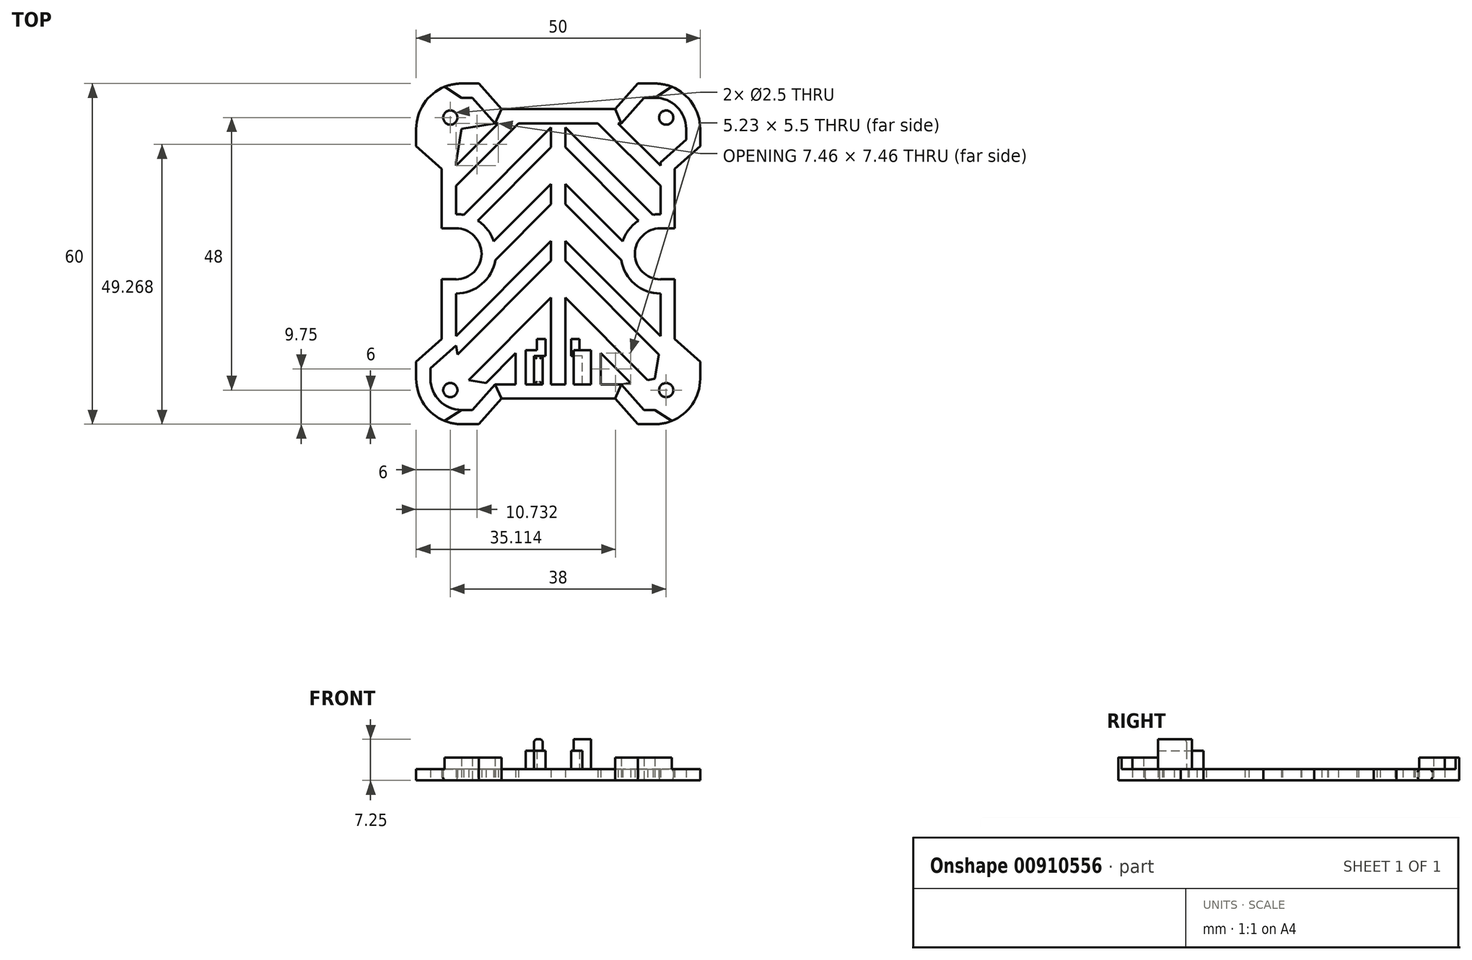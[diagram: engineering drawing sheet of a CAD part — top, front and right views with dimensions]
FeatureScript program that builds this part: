
annotation { "Feature Type Name" : "Feature", "Feature Type Description" : "" }
export const myFeature = defineFeature(function(context is Context, id is Id, definition is map)
    precondition{}
    {
        {
            var Q0;
            Q0=qCreatedBy(makeId("Top.planeOp"),FACE);
            var sketch = newSketch(context, id + "F0", { "sketchPlane" : qUnion([Q0])});
            skPoint(sketch, "E0.visualSharp", {"position": v(-25, 30) * mm});
            skArc(sketch, "E0.filletArc", {"start": v(-17, 30) * mm, "mid": v(-22.66, 27.66) * mm, "end": v(-25, 22) * mm});
            skPoint(sketch, "E1.visualSharp", {"position": v(25, 30) * mm});
            skArc(sketch, "E1.filletArc", {"start": v(25, 22) * mm, "mid": v(22.66, 27.66) * mm, "end": v(17, 30) * mm});
            skPoint(sketch, "E2.visualSharp", {"position": v(25, -30) * mm});
            skArc(sketch, "E2.filletArc", {"start": v(17, -30) * mm, "mid": v(22.66, -27.66) * mm, "end": v(25, -22) * mm});
            skPoint(sketch, "E3.visualSharp", {"position": v(-25, -30) * mm});
            skArc(sketch, "E3.filletArc", {"start": v(-25, -22) * mm, "mid": v(-22.66, -27.66) * mm, "end": v(-17, -30) * mm});
            skCircle(sketch, "E4", {"center": v(-19, 24) * mm, "radius": 1.25 * mm});
            skCircle(sketch, "E5.MirrorC", {"center": v(19, 24) * mm, "radius": 1.25 * mm});
            skCircle(sketch, "E6.MirrorC", {"center": v(19, -24) * mm, "radius": 1.25 * mm});
            skCircle(sketch, "E7.MirrorC", {"center": v(-19, -24) * mm, "radius": 1.25 * mm});
            skLineSegment(sketch, "E8", {"start": v(-10, 25.5) * mm, "end": v(10, 25.5) * mm});
            skLineSegment(sketch, "E9", {"start": v(-17, 30) * mm, "end": v(-14, 30) * mm});
            skLineSegment(sketch, "E10", {"start": v(-10, 25.5) * mm, "end": v(-14, 30) * mm});
            skLineSegment(sketch, "E11", {"start": v(10, 25.5) * mm, "end": v(14, 30) * mm});
            skLineSegment(sketch, "E12", {"start": v(-10, -25.5) * mm, "end": v(10, -25.5) * mm});
            skLineSegment(sketch, "E13", {"start": v(-17, -30) * mm, "end": v(-14, -30) * mm});
            skLineSegment(sketch, "E14", {"start": v(14, 30) * mm, "end": v(17, 30) * mm});
            skLineSegment(sketch, "E15", {"start": v(-14, -30) * mm, "end": v(-10, -25.5) * mm});
            skLineSegment(sketch, "E16", {"start": v(17, -30) * mm, "end": v(14, -30) * mm});
            skLineSegment(sketch, "E17", {"start": v(14, -30) * mm, "end": v(10, -25.5) * mm});
            skLineSegment(sketch, "E18", {"start": v(-25, -22) * mm, "end": v(-25, -19) * mm});
            skLineSegment(sketch, "E19", {"start": v(-25, 22) * mm, "end": v(-25, 19) * mm});
            skLineSegment(sketch, "E20", {"start": v(25, 22) * mm, "end": v(25, 19) * mm});
            skLineSegment(sketch, "E21", {"start": v(25, -22) * mm, "end": v(25, -19) * mm});
            skLineSegment(sketch, "E22", {"start": v(-20.5, -15) * mm, "end": v(-20.5, 15) * mm});
            skLineSegment(sketch, "E23", {"start": v(-25, -19) * mm, "end": v(-20.5, -15) * mm});
            skLineSegment(sketch, "E24", {"start": v(-20.5, 15) * mm, "end": v(-25, 19) * mm});
            skLineSegment(sketch, "E25", {"start": v(20.5, -15) * mm, "end": v(20.5, 15) * mm});
            skLineSegment(sketch, "E26", {"start": v(20.5, 15) * mm, "end": v(25, 19) * mm});
            skLineSegment(sketch, "E27", {"start": v(20.5, -15) * mm, "end": v(25, -19) * mm});
            skLineSegment(sketch, "E28", {"start": v(-10, -25.5) * mm, "end": v(-20.5, -15) * mm, "construction": true});
            skLineSegment(sketch, "E29", {"start": v(10, -25.5) * mm, "end": v(20.5, -15) * mm, "construction": true});
            skLineSegment(sketch, "E30", {"start": v(-20.5, 15) * mm, "end": v(-10, 25.5) * mm, "construction": true});
            skLineSegment(sketch, "E31", {"start": v(20.5, 15) * mm, "end": v(10, 25.5) * mm, "construction": true});
            skLineSegment(sketch, "E32.0", {"start": v(-11.12, 23) * mm, "end": v(-15.12, 27.5) * mm});
            skLineSegment(sketch, "E32.1", {"start": v(17, -27.5) * mm, "end": v(15.12, -27.5) * mm});
            skArc(sketch, "E32.2", {"start": v(17, -27.5) * mm, "mid": v(20.89, -25.89) * mm, "end": v(22.5, -22) * mm});
            skLineSegment(sketch, "E32.3", {"start": v(22.5, -22) * mm, "end": v(22.5, -20.12) * mm});
            skLineSegment(sketch, "E32.4", {"start": v(18, -16.12) * mm, "end": v(22.5, -20.12) * mm});
            skLineSegment(sketch, "E32.5", {"start": v(18, -16.12) * mm, "end": v(18, 16.12) * mm});
            skLineSegment(sketch, "E32.6", {"start": v(18, 16.12) * mm, "end": v(22.5, 20.12) * mm});
            skLineSegment(sketch, "E32.7", {"start": v(11.12, 23) * mm, "end": v(15.12, 27.5) * mm});
            skLineSegment(sketch, "E32.8", {"start": v(15.12, 27.5) * mm, "end": v(17, 27.5) * mm});
            skArc(sketch, "E32.9", {"start": v(22.5, 22) * mm, "mid": v(20.89, 25.89) * mm, "end": v(17, 27.5) * mm});
            skLineSegment(sketch, "E32.10", {"start": v(22.5, 22) * mm, "end": v(22.5, 20.12) * mm});
            skLineSegment(sketch, "E32.11", {"start": v(15.12, -27.5) * mm, "end": v(11.12, -23) * mm});
            skLineSegment(sketch, "E32.12", {"start": v(-11.12, 23) * mm, "end": v(11.12, 23) * mm});
            skLineSegment(sketch, "E32.13", {"start": v(-11.12, -23) * mm, "end": v(11.12, -23) * mm});
            skLineSegment(sketch, "E32.14", {"start": v(-15.12, -27.5) * mm, "end": v(-11.12, -23) * mm});
            skLineSegment(sketch, "E32.15", {"start": v(-17, -27.5) * mm, "end": v(-15.12, -27.5) * mm});
            skArc(sketch, "E32.16", {"start": v(-22.5, -22) * mm, "mid": v(-20.89, -25.89) * mm, "end": v(-17, -27.5) * mm});
            skLineSegment(sketch, "E32.17", {"start": v(-22.5, -22) * mm, "end": v(-22.5, -20.12) * mm});
            skLineSegment(sketch, "E32.18", {"start": v(-22.5, -20.12) * mm, "end": v(-18, -16.12) * mm});
            skLineSegment(sketch, "E32.19", {"start": v(-18, -16.12) * mm, "end": v(-18, 16.12) * mm});
            skLineSegment(sketch, "E32.20", {"start": v(-18, 16.12) * mm, "end": v(-22.5, 20.12) * mm});
            skLineSegment(sketch, "E32.21", {"start": v(-22.5, 22) * mm, "end": v(-22.5, 20.12) * mm});
            skArc(sketch, "E32.22", {"start": v(-17, 27.5) * mm, "mid": v(-20.89, 25.89) * mm, "end": v(-22.5, 22) * mm});
            skLineSegment(sketch, "E32.23", {"start": v(-17, 27.5) * mm, "end": v(-15.12, 27.5) * mm});
            skLineSegment(sketch, "E33", {"start": v(-18, 16.12) * mm, "end": v(-17, 22) * mm});
            skLineSegment(sketch, "E34", {"start": v(-11.12, 23) * mm, "end": v(-17, 22) * mm});
            skLineSegment(sketch, "E35", {"start": v(11.12, 23) * mm, "end": v(17, 22) * mm});
            skLineSegment(sketch, "E36", {"start": v(18, 16.12) * mm, "end": v(17, 22) * mm});
            skLineSegment(sketch, "E37", {"start": v(-11.12, -23) * mm, "end": v(-17, -22) * mm});
            skLineSegment(sketch, "E38", {"start": v(-18, -16.12) * mm, "end": v(-17, -22) * mm});
            skLineSegment(sketch, "E39", {"start": v(11.12, -23) * mm, "end": v(17, -22) * mm});
            skLineSegment(sketch, "E40", {"start": v(18, -16.12) * mm, "end": v(17, -22) * mm});
            skLineSegment(sketch, "E41", {"start": v(0, 3.54) * mm, "end": v(-18, -14.46) * mm});
            skLineSegment(sketch, "E42", {"start": v(0, 3.54) * mm, "end": v(18, -14.46) * mm});
            skLineSegment(sketch, "E43.0", {"start": v(-1.25, -1.25) * mm, "end": v(-17.75, -17.75) * mm});
            skLineSegment(sketch, "E43.1", {"start": v(1.25, -1.25) * mm, "end": v(17.75, -17.75) * mm});
            skLineSegment(sketch, "E44.0.1.0", {"start": v(1.25, 12.29) * mm, "end": v(18, -4.46) * mm});
            skLineSegment(sketch, "E44.0.1.1", {"start": v(1.25, 8.75) * mm, "end": v(18, -8) * mm});
            skLineSegment(sketch, "E44.0.1.2", {"start": v(-1.25, 8.75) * mm, "end": v(-18, -8) * mm});
            skLineSegment(sketch, "E44.0.1.3", {"start": v(-1.25, 12.29) * mm, "end": v(-18, -4.46) * mm});
            skLineSegment(sketch, "E44.0.2.0", {"start": v(1.25, 22.29) * mm, "end": v(18, 5.54) * mm});
            skLineSegment(sketch, "E44.0.2.1", {"start": v(1.25, 18.75) * mm, "end": v(18, 2) * mm});
            skLineSegment(sketch, "E44.0.2.2", {"start": v(-1.25, 18.75) * mm, "end": v(-18, 2) * mm});
            skLineSegment(sketch, "E44.0.2.3", {"start": v(-1.25, 22.29) * mm, "end": v(-18, 5.54) * mm});
            skLineSegment(sketch, "E44.0.3.2", {"start": v(-7, 23) * mm, "end": v(-18, 12) * mm});
            skLineSegment(sketch, "E44.0.3.3", {"start": v(-10.54, 23) * mm, "end": v(-18, 15.54) * mm});
            skLineSegment(sketch, "E44.direction1", {"start": v(18, -14.46) * mm, "end": v(43, -14.46) * mm, "construction": true});
            skLineSegment(sketch, "E44.direction2", {"start": v(18, -14.46) * mm, "end": v(18, -4.46) * mm, "construction": true});
            skLineSegment(sketch, "E45.0.1.0", {"start": v(1.25, -11.25) * mm, "end": v(12.75, -22.75) * mm});
            skLineSegment(sketch, "E45.0.1.1", {"start": v(1.25, -7.71) * mm, "end": v(15.75, -22.21) * mm});
            skLineSegment(sketch, "E45.0.1.2", {"start": v(-1.25, -7.71) * mm, "end": v(-15.75, -22.21) * mm});
            skLineSegment(sketch, "E45.0.1.3", {"start": v(-1.25, -11.25) * mm, "end": v(-12.75, -22.75) * mm});
            skLineSegment(sketch, "E45.0.2.0", {"start": v(1.25, -21.25) * mm, "end": v(3, -23) * mm});
            skLineSegment(sketch, "E45.0.2.1", {"start": v(1.25, -17.71) * mm, "end": v(6.54, -23) * mm});
            skLineSegment(sketch, "E45.0.2.2", {"start": v(-1.25, -17.71) * mm, "end": v(-6.54, -23) * mm});
            skLineSegment(sketch, "E45.0.2.3", {"start": v(-1.25, -21.25) * mm, "end": v(-3, -23) * mm});
            skLineSegment(sketch, "E45.direction1", {"start": v(18, -18) * mm, "end": v(43, -18) * mm, "construction": true});
            skLineSegment(sketch, "E45.direction2", {"start": v(18, -18) * mm, "end": v(18, -28) * mm, "construction": true});
            skPoint(sketch, "E46.orphan", {"position": v(-18, -34.46) * mm});
            skPoint(sketch, "E47.orphan", {"position": v(-18, -38) * mm});
            skPoint(sketch, "E48.orphan", {"position": v(18, -34.46) * mm});
            skLineSegment(sketch, "E49.trimOffspring", {"start": v(7, 23) * mm, "end": v(18, 12) * mm});
            skLineSegment(sketch, "E50.trimOffspring", {"start": v(10.54, 23) * mm, "end": v(18, 15.54) * mm});
            skPoint(sketch, "E51.orphan", {"position": v(0, 30) * mm});
            skPoint(sketch, "E52.orphan", {"position": v(0, 33.54) * mm});
            skPoint(sketch, "E53.orphan", {"position": v(0, 23.54) * mm});
            skLineSegment(sketch, "E54.bottom", {"start": v(-1.25, 23) * mm, "end": v(1.25, 23) * mm});
            skLineSegment(sketch, "E54.top", {"start": v(-1.25, -23) * mm, "end": v(1.25, -23) * mm});
            skLineSegment(sketch, "E54.left", {"start": v(-1.25, 23) * mm, "end": v(-1.25, -23) * mm});
            skLineSegment(sketch, "E54.right", {"start": v(1.25, 23) * mm, "end": v(1.25, -23) * mm});
            skPoint(sketch, "E54.middle", {"position": v(0, 0) * mm});
            skPoint(sketch, "E55.orphan", {"position": v(0, 20) * mm});
            skPoint(sketch, "E56.orphan", {"position": v(0, 13.54) * mm});
            skPoint(sketch, "E57.orphan", {"position": v(0, 10) * mm});
            skPoint(sketch, "E58.orphan", {"position": v(0, -20) * mm});
            skPoint(sketch, "E59.orphan", {"position": v(0, -16.46) * mm});
            skPoint(sketch, "E60.orphan", {"position": v(0, -10) * mm});
            skPoint(sketch, "E61.orphan", {"position": v(0, -6.46) * mm});
            skLineSegment(sketch, "E62", {"start": v(-7.5, -23) * mm, "end": v(-7.5, -17.5) * mm});
            skLineSegment(sketch, "E63.MirrorCS", {"start": v(7.5, -23) * mm, "end": v(7.5, -17.5) * mm});
            skLineSegment(sketch, "E64", {"start": v(-11.12, 23) * mm, "end": v(-10, 25.5) * mm});
            skLineSegment(sketch, "E65", {"start": v(-17, 27.5) * mm, "end": v(-20, 29.42) * mm});
            skLineSegment(sketch, "E66", {"start": v(11.12, 23) * mm, "end": v(10, 25.5) * mm});
            skLineSegment(sketch, "E67", {"start": v(17, 27.5) * mm, "end": v(20, 29.42) * mm});
            skLineSegment(sketch, "E68", {"start": v(-10, -25.5) * mm, "end": v(-11.12, -23) * mm});
            skLineSegment(sketch, "E69", {"start": v(10, -25.5) * mm, "end": v(11.12, -23) * mm});
            skLineSegment(sketch, "E70", {"start": v(-17, -27.5) * mm, "end": v(-20, -29.42) * mm});
            skLineSegment(sketch, "E71", {"start": v(17, -27.5) * mm, "end": v(20, -29.42) * mm});
            skArc(sketch, "E72.trimOffspring", {"start": v(-18, -7) * mm, "mid": v(-11, 0) * mm, "end": v(-18, 7) * mm});
            skArc(sketch, "E73.trimOffspring", {"start": v(-18, -4.5) * mm, "mid": v(-13.5, 0) * mm, "end": v(-18, 4.5) * mm});
            skLineSegment(sketch, "E74", {"start": v(-18, 7) * mm, "end": v(-20.5, 7) * mm});
            skLineSegment(sketch, "E75", {"start": v(-18, 4.5) * mm, "end": v(-20.5, 4.5) * mm});
            skLineSegment(sketch, "E76", {"start": v(-18, -7) * mm, "end": v(-20.5, -7) * mm});
            skLineSegment(sketch, "E77", {"start": v(-18, -4.46) * mm, "end": v(-20.5, -4.46) * mm});
            skArc(sketch, "E78.MirrorCS", {"start": v(18, -4.5) * mm, "mid": v(13.5, 0) * mm, "end": v(18, 4.5) * mm});
            skArc(sketch, "E79.MirrorCS", {"start": v(18, -7) * mm, "mid": v(11, 0) * mm, "end": v(18, 7) * mm});
            skLineSegment(sketch, "E80.MirrorCS", {"start": v(18, 4.5) * mm, "end": v(20.5, 4.5) * mm});
            skLineSegment(sketch, "E81.MirrorCS", {"start": v(18, 7) * mm, "end": v(20.5, 7) * mm});
            skLineSegment(sketch, "E82.MirrorCS", {"start": v(18, -7) * mm, "end": v(20.5, -7) * mm});
            skLineSegment(sketch, "E83.MirrorCS", {"start": v(18, -4.46) * mm, "end": v(20.5, -4.46) * mm});
            skSolve(sketch);
        }
        {
            var Q0;
            Q0=makeQuery(id+"F0.imprint","IMPRINT",FACE,{"disambiguationData":[TD([[makeQuery(id+"F0.imprint","IMPRINT",EDGE,{"derivedFrom":sQuery(id+"F0.wireOp",EDGE,"qVhlgd7Z-K8wA-2s9c-4Va0-7I31SFR7jzgF.bottom")}),-1.0]])]});
            var Q1;
            {var subQ1=sQuery(id+"F0.wireOp",EDGE,"bAQaguaC-gw7z-6hSp-WNjj-it6Kwomhn3MH.bottom");var subQ4=sQuery(id+"F0.wireOp",EDGE,"bAQaguaC-gw7z-6hSp-WNjj-it6Kwomhn3MH.left");var subQ9=makeQuery(id+"F0.imprint","INTERSECT",VERTEX,{"derivedFrom":[subQ1,subQ4]});Q1=makeQuery(id+"F0.imprint","IMPRINT",FACE,{"disambiguationData":[TD([[makeQuery(id+"F0.imprint","IMPRINT",EDGE,{"disambiguationData":[TD([[subQ9,-1.0]])],"derivedFrom":subQ1}),-1.0]])]});}
            var Q2;
            {var subQ0=sQuery(id+"F0.wireOp",EDGE,"3b41a42e-ea02-44ec-bd11-05c8cb4d84110.MirrorCS");Q2=makeQuery(id+"F0.imprint","IMPRINT",FACE,{"disambiguationData":[TD([[makeQuery(id+"F0.imprint","IMPRINT",EDGE,{"derivedFrom":subQ0}),-1.0]])]});}
            var Q3;
            Q3=makeQuery(id+"F0.imprint","IMPRINT",FACE,{"disambiguationData":[TD([[makeQuery(id+"F0.imprint","IMPRINT",EDGE,{"derivedFrom":sQuery(id+"F0.wireOp",EDGE,"5EblEZfn-I8Wa-IbvZ-PO4Y-9xLoYuIDBuYk.bottom")}),-1.0]])]});
            var Q4;
            {var subQ0=sQuery(id+"F0.wireOp",EDGE,"252a318b-4038-41aa-b63b-639a4f701ae30.MirrorCS");Q4=makeQuery(id+"F0.imprint","IMPRINT",FACE,{"disambiguationData":[TD([[makeQuery(id+"F0.imprint","IMPRINT",EDGE,{"derivedFrom":subQ0}),1.0]])]});}
            var Q5;
            {var subQ0=sQuery(id+"F0.wireOp",EDGE,"58b98b9d-614e-4e5d-8269-9d4372af3b9f0.MirrorCS");Q5=makeQuery(id+"F0.imprint","IMPRINT",FACE,{"disambiguationData":[TD([[makeQuery(id+"F0.imprint","IMPRINT",EDGE,{"derivedFrom":subQ0}),-1.0]])]});}
            var Q6;
            Q6=makeQuery(id+"F0.imprint","IMPRINT",FACE,{"disambiguationData":[TD([[makeQuery(id+"F0.imprint","IMPRINT",EDGE,{"derivedFrom":sQuery(id+"F0.wireOp",EDGE,"E0.filletArc")}),1.0]])]});
            var Q7;
            Q7=makeQuery(id+"F0.imprint","IMPRINT",FACE,{"disambiguationData":[TD([[makeQuery(id+"F0.imprint","IMPRINT",EDGE,{"derivedFrom":sQuery(id+"F0.wireOp",EDGE,"xvgLrtku-wdkR-8HBo-YxuC-FjmSOnXhvL37")}),-1.0]])]});
            var Q8;
            Q8=makeQuery(id+"F0.imprint","IMPRINT",FACE,{"disambiguationData":[TD([[makeQuery(id+"F0.imprint","IMPRINT",EDGE,{"derivedFrom":sQuery(id+"F0.wireOp",EDGE,"E10")}),1.0]])]});
            var Q9;
            Q9=makeQuery(id+"F0.imprint","IMPRINT",FACE,{"disambiguationData":[TD([[makeQuery(id+"F0.imprint","IMPRINT",EDGE,{"derivedFrom":sQuery(id+"F0.wireOp",EDGE,"5909cff1-2e5d-4e63-b456-f55076b46f4d0.MirrorCS")}),-1.0]])]});
            var Q10;
            Q10=makeQuery(id+"F0.imprint","IMPRINT",FACE,{"disambiguationData":[TD([[makeQuery(id+"F0.imprint","IMPRINT",EDGE,{"derivedFrom":sQuery(id+"F0.wireOp",EDGE,"86012b31-d1bc-4a6e-bdbf-ee867ae8a5b00.MirrorCS")}),1.0]])]});
            var Q11;
            Q11=makeQuery(id+"F0.imprint","IMPRINT",FACE,{"disambiguationData":[TD([[makeQuery(id+"F0.imprint","IMPRINT",EDGE,{"derivedFrom":sQuery(id+"F0.wireOp",EDGE,"afaa9ab5-ff9c-4d97-af4b-f4bc579a4ab80.MirrorCS")}),-1.0]])]});
            var Q12;
            {var subQ0=sQuery(id+"F0.wireOp",EDGE,"E44.0.3.2");Q12=makeQuery(id+"F0.imprint","IMPRINT",FACE,{"disambiguationData":[TD([[makeQuery(id+"F0.imprint","IMPRINT",EDGE,{"derivedFrom":subQ0}),-1.0]])]});}
            var Q13;
            {var subQ0=sQuery(id+"F0.wireOp",EDGE,"E49.trimOffspring");Q13=makeQuery(id+"F0.imprint","IMPRINT",FACE,{"disambiguationData":[TD([[makeQuery(id+"F0.imprint","IMPRINT",EDGE,{"derivedFrom":subQ0}),1.0]])]});}
            var Q14;
            {var subQ0=sQuery(id+"F0.wireOp",EDGE,"E45.0.1.1");Q14=makeQuery(id+"F0.imprint","IMPRINT",FACE,{"disambiguationData":[TD([[makeQuery(id+"F0.imprint","IMPRINT",EDGE,{"derivedFrom":subQ0}),-1.0]])]});}
            var Q15;
            {var subQ1=sQuery(id+"F0.wireOp",EDGE,"E45.0.2.0");Q15=makeQuery(id+"F0.imprint","IMPRINT",FACE,{"disambiguationData":[TD([[makeQuery(id+"F0.imprint","IMPRINT",EDGE,{"derivedFrom":subQ1}),1.0]])]});}
            var Q16;
            {var subQ3=sQuery(id+"F0.wireOp",EDGE,"E41");Q16=makeQuery(id+"F0.imprint","IMPRINT",FACE,{"disambiguationData":[TD([[makeQuery(id+"F0.imprint","IMPRINT",EDGE,{"derivedFrom":subQ3}),1.0]])]});}
            var Q17;
            {var subQ0=sQuery(id+"F0.wireOp",EDGE,"E44.0.2.0");Q17=makeQuery(id+"F0.imprint","IMPRINT",FACE,{"disambiguationData":[TD([[makeQuery(id+"F0.imprint","IMPRINT",EDGE,{"derivedFrom":subQ0}),-1.0]])]});}
            var Q18;
            Q18=makeQuery(id+"F0.imprint","IMPRINT",FACE,{"disambiguationData":[TD([[makeQuery(id+"F0.imprint","IMPRINT",EDGE,{"derivedFrom":sQuery(id+"F0.wireOp",EDGE,"E6.MirrorC")}),-1.0]])]});
            var Q19;
            Q19=makeQuery(id+"F0.imprint","IMPRINT",FACE,{"disambiguationData":[TD([[makeQuery(id+"F0.imprint","IMPRINT",EDGE,{"derivedFrom":sQuery(id+"F0.wireOp",EDGE,"E5.MirrorC")}),1.0]])]});
            var Q20;
            Q20=makeQuery(id+"F0.imprint","IMPRINT",FACE,{"disambiguationData":[TD([[makeQuery(id+"F0.imprint","IMPRINT",EDGE,{"derivedFrom":sQuery(id+"F0.wireOp",EDGE,"E4")}),-1.0]])]});
            var Q21;
            Q21=makeQuery(id+"F0.imprint","IMPRINT",FACE,{"disambiguationData":[TD([[makeQuery(id+"F0.imprint","IMPRINT",EDGE,{"derivedFrom":sQuery(id+"F0.wireOp",EDGE,"E7.MirrorC")}),1.0]])]});
            var Q22;
            {var subQ13=sQuery(id+"F0.wireOp",EDGE,"E54.top");Q22=makeQuery(id+"F0.imprint","IMPRINT",FACE,{"disambiguationData":[TD([[makeQuery(id+"F0.imprint","IMPRINT",EDGE,{"derivedFrom":subQ13}),1.0]])]});}
            var Q23;
            {var subQ5=sQuery(id+"F0.wireOp",EDGE,"E42");var subQ6=sQuery(id+"F0.wireOp",EDGE,"E32.5");var subQ7=makeQuery(id+"F0.imprint","INTERSECT",VERTEX,{"derivedFrom":[subQ6,subQ5]});Q23=makeQuery(id+"F0.imprint","IMPRINT",FACE,{"disambiguationData":[TD([[makeQuery(id+"F0.imprint","IMPRINT",EDGE,{"disambiguationData":[TD([[subQ7,1.0]])],"derivedFrom":subQ5}),-1.0]])]});}
            var Q24;
            {var subQ0=sQuery(id+"F0.wireOp",EDGE,"E45.0.1.2");Q24=makeQuery(id+"F0.imprint","IMPRINT",FACE,{"disambiguationData":[TD([[makeQuery(id+"F0.imprint","IMPRINT",EDGE,{"derivedFrom":subQ0}),1.0]])]});}
            var Q25;
            {var subQ0=sQuery(id+"F0.wireOp",EDGE,"E45.0.2.2");Q25=makeQuery(id+"F0.imprint","IMPRINT",FACE,{"disambiguationData":[TD([[makeQuery(id+"F0.imprint","IMPRINT",EDGE,{"derivedFrom":subQ0}),1.0]])]});}
            var Q26;
            {var subQ0=sQuery(id+"F0.wireOp",EDGE,"E45.0.2.3");Q26=makeQuery(id+"F0.imprint","IMPRINT",FACE,{"disambiguationData":[TD([[makeQuery(id+"F0.imprint","IMPRINT",EDGE,{"derivedFrom":subQ0}),1.0]])]});}
            var Q27;
            {var subQ0=sQuery(id+"F0.wireOp",EDGE,"E45.0.2.0");Q27=makeQuery(id+"F0.imprint","IMPRINT",FACE,{"disambiguationData":[TD([[makeQuery(id+"F0.imprint","IMPRINT",EDGE,{"derivedFrom":subQ0}),-1.0]])]});}
            var Q28;
            {var subQ13=sQuery(id+"F0.wireOp",EDGE,"E54.bottom");Q28=makeQuery(id+"F0.imprint","IMPRINT",FACE,{"disambiguationData":[TD([[makeQuery(id+"F0.imprint","IMPRINT",EDGE,{"derivedFrom":subQ13}),-1.0]])]});}
            var Q29;
            {var subQ4=sQuery(id+"F0.wireOp",EDGE,"E45.0.2.1");Q29=makeQuery(id+"F0.imprint","IMPRINT",FACE,{"disambiguationData":[TD([[makeQuery(id+"F0.imprint","IMPRINT",EDGE,{"derivedFrom":subQ4}),1.0]])]});}
            var Q30;
            {var subQ4=sQuery(id+"F0.wireOp",EDGE,"E45.0.2.2");Q30=makeQuery(id+"F0.imprint","IMPRINT",FACE,{"disambiguationData":[TD([[makeQuery(id+"F0.imprint","IMPRINT",EDGE,{"derivedFrom":subQ4}),-1.0]])]});}
            var Q31;
            {var subQ11=sQuery(id+"F0.wireOp",EDGE,"E18");Q31=makeQuery(id+"F0.imprint","IMPRINT",FACE,{"disambiguationData":[TD([[makeQuery(id+"F0.imprint","IMPRINT",EDGE,{"derivedFrom":subQ11}),-1.0]])]});}
            var Q32;
            Q32=makeQuery(id+"F0.imprint","IMPRINT",FACE,{"disambiguationData":[TD([[makeQuery(id+"F0.imprint","IMPRINT",EDGE,{"derivedFrom":sQuery(id+"F0.wireOp",EDGE,"E8")}),-1.0]])]});
            var Q33;
            {var subQ0=sQuery(id+"F0.wireOp",EDGE,"E20");Q33=makeQuery(id+"F0.imprint","IMPRINT",FACE,{"disambiguationData":[TD([[makeQuery(id+"F0.imprint","IMPRINT",EDGE,{"derivedFrom":subQ0}),-1.0]])]});}
            var Q34;
            Q34=makeQuery(id+"F0.imprint","IMPRINT",FACE,{"disambiguationData":[TD([[makeQuery(id+"F0.imprint","IMPRINT",EDGE,{"derivedFrom":sQuery(id+"F0.wireOp",EDGE,"E12")}),1.0]])]});
            var Q35;
            Q35=makeQuery(id+"F0.imprint","IMPRINT",FACE,{"disambiguationData":[TD([[makeQuery(id+"F0.imprint","IMPRINT",EDGE,{"derivedFrom":sQuery(id+"F0.wireOp",EDGE,"E11")}),-1.0]])]});
            var Q36;
            {var subQ0=sQuery(id+"F0.wireOp",EDGE,"E16");Q36=makeQuery(id+"F0.imprint","IMPRINT",FACE,{"disambiguationData":[TD([[makeQuery(id+"F0.imprint","IMPRINT",EDGE,{"derivedFrom":subQ0}),-1.0]])]});}
            var Q37;
            {var subQ0=sQuery(id+"F0.wireOp",EDGE,"E13");Q37=makeQuery(id+"F0.imprint","IMPRINT",FACE,{"disambiguationData":[TD([[makeQuery(id+"F0.imprint","IMPRINT",EDGE,{"derivedFrom":subQ0}),1.0]])]});}
            var Q38;
            {var subQ3=sQuery(id+"F0.wireOp",EDGE,"E19");Q38=makeQuery(id+"F0.imprint","IMPRINT",FACE,{"disambiguationData":[TD([[makeQuery(id+"F0.imprint","IMPRINT",EDGE,{"derivedFrom":subQ3}),1.0]])]});}
            var Q39;
            {var subQ4=sQuery(id+"F0.wireOp",EDGE,"E21");Q39=makeQuery(id+"F0.imprint","IMPRINT",FACE,{"disambiguationData":[TD([[makeQuery(id+"F0.imprint","IMPRINT",EDGE,{"derivedFrom":subQ4}),1.0]])]});}
            var Q40;
            {var subQ0=sQuery(id+"F0.wireOp",EDGE,"E82.MirrorCS");Q40=makeQuery(id+"F0.imprint","IMPRINT",FACE,{"disambiguationData":[TD([[makeQuery(id+"F0.imprint","IMPRINT",EDGE,{"derivedFrom":subQ0}),1.0]])]});}
            var Q41;
            {var subQ0=sQuery(id+"F0.wireOp",EDGE,"E44.0.2.0");var subQ1=sQuery(id+"F0.wireOp",EDGE,"E32.5");var subQ2=makeQuery(id+"F0.imprint","INTERSECT",VERTEX,{"derivedFrom":[subQ1,subQ0]});Q41=makeQuery(id+"F0.imprint","IMPRINT",FACE,{"disambiguationData":[TD([[makeQuery(id+"F0.imprint","IMPRINT",EDGE,{"disambiguationData":[TD([[subQ2,1.0]])],"derivedFrom":subQ0}),1.0]])]});}
            var Q42;
            {var subQ1=sQuery(id+"F0.wireOp",EDGE,"E32.5");var subQ7=sQuery(id+"F0.wireOp",EDGE,"E44.0.2.0");var subQ8=makeQuery(id+"F0.imprint","INTERSECT",VERTEX,{"derivedFrom":[subQ1,subQ7]});Q42=makeQuery(id+"F0.imprint","IMPRINT",FACE,{"disambiguationData":[TD([[makeQuery(id+"F0.imprint","IMPRINT",EDGE,{"disambiguationData":[TD([[subQ8,1.0]])],"derivedFrom":subQ7}),-1.0]])]});}
            var Q43;
            {var subQ0=sQuery(id+"F0.wireOp",EDGE,"E79.MirrorCS");var subQ1=sQuery(id+"F0.wireOp",EDGE,"E44.0.1.0");var subQ2=makeQuery(id+"F0.imprint","INTERSECT",VERTEX,{"derivedFrom":[subQ1,subQ0]});Q43=makeQuery(id+"F0.imprint","IMPRINT",FACE,{"disambiguationData":[TD([[makeQuery(id+"F0.imprint","IMPRINT",EDGE,{"disambiguationData":[TD([[subQ2,-1.0]])],"derivedFrom":subQ1}),1.0]])]});}
            var Q44;
            {var subQ3=sQuery(id+"F0.wireOp",EDGE,"E44.0.1.0");var subQ5=sQuery(id+"F0.wireOp",EDGE,"E79.MirrorCS");var subQ9=makeQuery(id+"F0.imprint","INTERSECT",VERTEX,{"derivedFrom":[subQ3,subQ5]});Q44=makeQuery(id+"F0.imprint","IMPRINT",FACE,{"disambiguationData":[TD([[makeQuery(id+"F0.imprint","IMPRINT",EDGE,{"disambiguationData":[TD([[subQ9,-1.0]])],"derivedFrom":subQ3}),-1.0]])]});}
            var Q45;
            {var subQ0=sQuery(id+"F0.wireOp",EDGE,"E79.MirrorCS");var subQ1=sQuery(id+"F0.wireOp",EDGE,"E44.0.1.1");var subQ2=makeQuery(id+"F0.imprint","INTERSECT",VERTEX,{"disambiguationData":[OD(0.0)],"derivedFrom":[subQ1,subQ0]});Q45=makeQuery(id+"F0.imprint","IMPRINT",FACE,{"disambiguationData":[TD([[makeQuery(id+"F0.imprint","IMPRINT",EDGE,{"disambiguationData":[TD([[subQ2,-1.0]])],"derivedFrom":subQ1}),-1.0]])]});}
            var Q46;
            {var subQ0=sQuery(id+"F0.wireOp",EDGE,"E80.MirrorCS");Q46=makeQuery(id+"F0.imprint","IMPRINT",FACE,{"disambiguationData":[TD([[makeQuery(id+"F0.imprint","IMPRINT",EDGE,{"derivedFrom":subQ0}),1.0]])]});}
            var Q47;
            {var subQ0=sQuery(id+"F0.wireOp",EDGE,"E54.left");var subQ1=sQuery(id+"F0.wireOp",EDGE,"E44.0.2.2");var subQ2=makeQuery(id+"F0.imprint","INTERSECT",VERTEX,{"derivedFrom":[subQ1,subQ0]});Q47=makeQuery(id+"F0.imprint","IMPRINT",FACE,{"disambiguationData":[TD([[makeQuery(id+"F0.imprint","IMPRINT",EDGE,{"disambiguationData":[TD([[subQ2,-1.0]])],"derivedFrom":subQ1}),-1.0]])]});}
            var Q48;
            {var subQ0=sQuery(id+"F0.wireOp",EDGE,"E54.right");var subQ1=sQuery(id+"F0.wireOp",EDGE,"E44.0.1.0");var subQ2=makeQuery(id+"F0.imprint","INTERSECT",VERTEX,{"derivedFrom":[subQ1,subQ0]});Q48=makeQuery(id+"F0.imprint","IMPRINT",FACE,{"disambiguationData":[TD([[makeQuery(id+"F0.imprint","IMPRINT",EDGE,{"disambiguationData":[TD([[subQ2,-1.0]])],"derivedFrom":subQ1}),-1.0]])]});}
            var Q49;
            {var subQ0=sQuery(id+"F0.wireOp",EDGE,"E72.trimOffspring");var subQ1=sQuery(id+"F0.wireOp",EDGE,"E44.0.1.3");var subQ2=makeQuery(id+"F0.imprint","INTERSECT",VERTEX,{"derivedFrom":[subQ1,subQ0]});Q49=makeQuery(id+"F0.imprint","IMPRINT",FACE,{"disambiguationData":[TD([[makeQuery(id+"F0.imprint","IMPRINT",EDGE,{"disambiguationData":[TD([[subQ2,-1.0]])],"derivedFrom":subQ1}),-1.0]])]});}
            var Q50;
            {var subQ0=sQuery(id+"F0.wireOp",EDGE,"E74");Q50=makeQuery(id+"F0.imprint","IMPRINT",FACE,{"disambiguationData":[TD([[makeQuery(id+"F0.imprint","IMPRINT",EDGE,{"derivedFrom":subQ0}),1.0]])]});}
            var Q51;
            {var subQ0=sQuery(id+"F0.wireOp",EDGE,"E54.left");var subQ1=sQuery(id+"F0.wireOp",EDGE,"E44.0.1.2");var subQ2=makeQuery(id+"F0.imprint","INTERSECT",VERTEX,{"derivedFrom":[subQ1,subQ0]});Q51=makeQuery(id+"F0.imprint","IMPRINT",FACE,{"disambiguationData":[TD([[makeQuery(id+"F0.imprint","IMPRINT",EDGE,{"disambiguationData":[TD([[subQ2,-1.0]])],"derivedFrom":subQ1}),-1.0]])]});}
            var Q52;
            {var subQ0=sQuery(id+"F0.wireOp",EDGE,"E44.0.2.3");var subQ1=sQuery(id+"F0.wireOp",EDGE,"E32.19");var subQ2=makeQuery(id+"F0.imprint","INTERSECT",VERTEX,{"derivedFrom":[subQ1,subQ0]});Q52=makeQuery(id+"F0.imprint","IMPRINT",FACE,{"disambiguationData":[TD([[makeQuery(id+"F0.imprint","IMPRINT",EDGE,{"disambiguationData":[TD([[subQ2,1.0]])],"derivedFrom":subQ0}),-1.0]])]});}
            var Q53;
            {var subQ0=sQuery(id+"F0.wireOp",EDGE,"E72.trimOffspring");var subQ1=sQuery(id+"F0.wireOp",EDGE,"E44.0.1.2");var subQ2=makeQuery(id+"F0.imprint","INTERSECT",VERTEX,{"disambiguationData":[OD(0.0)],"derivedFrom":[subQ1,subQ0]});Q53=makeQuery(id+"F0.imprint","IMPRINT",FACE,{"disambiguationData":[TD([[makeQuery(id+"F0.imprint","IMPRINT",EDGE,{"disambiguationData":[TD([[subQ2,-1.0]])],"derivedFrom":subQ1}),1.0]])]});}
            var Q54;
            {var subQ0=sQuery(id+"F0.wireOp",EDGE,"E72.trimOffspring");var subQ1=sQuery(id+"F0.wireOp",EDGE,"E44.0.2.2");var subQ2=makeQuery(id+"F0.imprint","INTERSECT",VERTEX,{"derivedFrom":[subQ1,subQ0]});Q54=makeQuery(id+"F0.imprint","IMPRINT",FACE,{"disambiguationData":[TD([[makeQuery(id+"F0.imprint","IMPRINT",EDGE,{"disambiguationData":[TD([[subQ2,-1.0]])],"derivedFrom":subQ1}),-1.0]])]});}
            var Q55;
            {var subQ0=sQuery(id+"F0.wireOp",EDGE,"E72.trimOffspring");var subQ3=sQuery(id+"F0.wireOp",EDGE,"E44.0.1.2");var subQ10=makeQuery(id+"F0.imprint","INTERSECT",VERTEX,{"disambiguationData":[OD(0.0)],"derivedFrom":[subQ3,subQ0]});Q55=makeQuery(id+"F0.imprint","IMPRINT",FACE,{"disambiguationData":[TD([[makeQuery(id+"F0.imprint","IMPRINT",EDGE,{"disambiguationData":[TD([[subQ10,-1.0]])],"derivedFrom":subQ3}),-1.0]])]});}
            var Q56;
            {var subQ0=sQuery(id+"F0.wireOp",EDGE,"E76");Q56=makeQuery(id+"F0.imprint","IMPRINT",FACE,{"disambiguationData":[TD([[makeQuery(id+"F0.imprint","IMPRINT",EDGE,{"derivedFrom":subQ0}),-1.0]])]});}
            extrude(context, id + "F1", {"entities" : qUnion([Q0, Q1, Q2, Q3, Q4, Q5, Q6, Q7, Q8, Q9, Q10, Q11, Q12, Q13, Q14, Q15, Q16, Q17, Q18, Q19, Q20, Q21, Q22, Q23, Q24, Q25, Q26, Q27, Q28, Q29, Q30, Q31, Q32, Q33, Q34, Q35, Q36, Q37, Q38, Q39, Q40, Q41, Q42, Q43, Q44, Q45, Q46, Q47, Q48, Q49, Q50, Q51, Q52, Q53, Q54, Q55, Q56]), "depth" : 2 * mm});
        }
        {
            var Q0;
            Q0=makeQuery(id+"F1.opExtrude","CAP_FACE",FACE,{"disambiguationData":[OSD([sQuery(id+"F0.wireOp",EDGE,"E0.filletArc"),sQuery(id+"F0.wireOp",EDGE,"E1.filletArc"),sQuery(id+"F0.wireOp",EDGE,"E2.filletArc"),sQuery(id+"F0.wireOp",EDGE,"E3.filletArc"),sQuery(id+"F0.wireOp",EDGE,"E4"),sQuery(id+"F0.wireOp",EDGE,"E5.MirrorC"),sQuery(id+"F0.wireOp",EDGE,"E6.MirrorC"),sQuery(id+"F0.wireOp",EDGE,"E7.MirrorC"),sQuery(id+"F0.wireOp",EDGE,"E8"),sQuery(id+"F0.wireOp",EDGE,"E9"),sQuery(id+"F0.wireOp",EDGE,"E10"),sQuery(id+"F0.wireOp",EDGE,"E11"),sQuery(id+"F0.wireOp",EDGE,"E12"),sQuery(id+"F0.wireOp",EDGE,"E13"),sQuery(id+"F0.wireOp",EDGE,"E14"),sQuery(id+"F0.wireOp",EDGE,"E15"),sQuery(id+"F0.wireOp",EDGE,"E16"),sQuery(id+"F0.wireOp",EDGE,"E17"),sQuery(id+"F0.wireOp",EDGE,"E18"),sQuery(id+"F0.wireOp",EDGE,"E19"),sQuery(id+"F0.wireOp",EDGE,"E20"),sQuery(id+"F0.wireOp",EDGE,"E21"),sQuery(id+"F0.wireOp",EDGE,"E22"),sQuery(id+"F0.wireOp",EDGE,"E23"),sQuery(id+"F0.wireOp",EDGE,"E24"),sQuery(id+"F0.wireOp",EDGE,"E25"),sQuery(id+"F0.wireOp",EDGE,"E26"),sQuery(id+"F0.wireOp",EDGE,"E27"),sQuery(id+"F0.wireOp",EDGE,"E32.5"),sQuery(id+"F0.wireOp",EDGE,"E32.12"),sQuery(id+"F0.wireOp",EDGE,"E32.13"),sQuery(id+"F0.wireOp",EDGE,"E32.19"),sQuery(id+"F0.wireOp",EDGE,"E33"),sQuery(id+"F0.wireOp",EDGE,"E34"),sQuery(id+"F0.wireOp",EDGE,"E35"),sQuery(id+"F0.wireOp",EDGE,"E36"),sQuery(id+"F0.wireOp",EDGE,"E37"),sQuery(id+"F0.wireOp",EDGE,"E38"),sQuery(id+"F0.wireOp",EDGE,"E39"),sQuery(id+"F0.wireOp",EDGE,"E40"),sQuery(id+"F0.wireOp",EDGE,"E41"),sQuery(id+"F0.wireOp",EDGE,"E42"),sQuery(id+"F0.wireOp",EDGE,"E43.0"),sQuery(id+"F0.wireOp",EDGE,"E43.1"),sQuery(id+"F0.wireOp",EDGE,"E44.0.1.0"),sQuery(id+"F0.wireOp",EDGE,"E44.0.1.1"),sQuery(id+"F0.wireOp",EDGE,"E44.0.1.2"),sQuery(id+"F0.wireOp",EDGE,"E44.0.1.3"),sQuery(id+"F0.wireOp",EDGE,"E44.0.2.0"),sQuery(id+"F0.wireOp",EDGE,"E44.0.2.1"),sQuery(id+"F0.wireOp",EDGE,"E44.0.2.2"),sQuery(id+"F0.wireOp",EDGE,"E44.0.2.3"),sQuery(id+"F0.wireOp",EDGE,"E44.0.3.2"),sQuery(id+"F0.wireOp",EDGE,"E44.0.3.3"),sQuery(id+"F0.wireOp",EDGE,"E45.0.1.0"),sQuery(id+"F0.wireOp",EDGE,"E45.0.1.1"),sQuery(id+"F0.wireOp",EDGE,"E45.0.1.2"),sQuery(id+"F0.wireOp",EDGE,"E45.0.1.3"),sQuery(id+"F0.wireOp",EDGE,"E45.0.2.1"),sQuery(id+"F0.wireOp",EDGE,"E45.0.2.2"),sQuery(id+"F0.wireOp",EDGE,"E49.trimOffspring"),sQuery(id+"F0.wireOp",EDGE,"E50.trimOffspring"),sQuery(id+"F0.wireOp",EDGE,"E54.left"),sQuery(id+"F0.wireOp",EDGE,"E54.right")])],"isStart":false});
            var sketch = newSketch(context, id + "F2", { "sketchPlane" : qUnion([Q0])});
            skLineSegment(sketch, "E84.bottom", {"start": v(5.75, -23) * mm, "end": v(5.75, -17) * mm});
            skLineSegment(sketch, "E84.top", {"start": v(4.25, -23) * mm, "end": v(4.25, -18) * mm});
            skLineSegment(sketch, "E84.left", {"start": v(5.75, -23) * mm, "end": v(4.25, -23) * mm});
            skLineSegment(sketch, "E84.right", {"start": v(5.75, -17) * mm, "end": v(4.25, -17) * mm});
            skLineSegment(sketch, "E85.left", {"start": v(4.25, -18) * mm, "end": v(3.75, -18) * mm});
            skLineSegment(sketch, "E85.right", {"start": v(4.25, -17) * mm, "end": v(3.75, -17) * mm});
            skLineSegment(sketch, "E86.bottom", {"start": v(3.75, -17) * mm, "end": v(3.75, -15) * mm});
            skLineSegment(sketch, "E86.top", {"start": v(2.25, -18) * mm, "end": v(2.25, -15) * mm});
            skLineSegment(sketch, "E86.left", {"start": v(3.75, -18) * mm, "end": v(2.25, -18) * mm});
            skLineSegment(sketch, "E86.right", {"start": v(3.75, -15) * mm, "end": v(2.25, -15) * mm});
            skPoint(sketch, "E87.visualSharp", {"position": v(3.75, -15) * mm});
            skPoint(sketch, "E88.visualSharp", {"position": v(2.25, -15) * mm});
            skPoint(sketch, "E89.visualSharp", {"position": v(2.25, -18) * mm});
            skPoint(sketch, "E90.visualSharp", {"position": v(4.25, -23) * mm});
            skPoint(sketch, "E91", {"position": v(5.75, -23) * mm});
            skPoint(sketch, "E92", {"position": v(5.75, -17) * mm});
            skLineSegment(sketch, "E93", {"start": v(2.25, -15) * mm, "end": v(-2.25, -15) * mm, "construction": true});
            skPoint(sketch, "E94", {"position": v(0, -15) * mm});
            skLineSegment(sketch, "E95", {"start": v(0, -15) * mm, "end": v(0, -25.74) * mm, "construction": true});
            skLineSegment(sketch, "E96.MirrorCS", {"start": v(-5.75, -23) * mm, "end": v(-4.25, -23) * mm});
            skLineSegment(sketch, "E97.MirrorCS", {"start": v(-5.75, -23) * mm, "end": v(-5.75, -17) * mm});
            skLineSegment(sketch, "E98.MirrorCS", {"start": v(-4.25, -17) * mm, "end": v(-3.75, -17) * mm});
            skLineSegment(sketch, "E99.MirrorCS", {"start": v(-5.75, -17) * mm, "end": v(-4.25, -17) * mm});
            skLineSegment(sketch, "E100.MirrorCS", {"start": v(-3.75, -18) * mm, "end": v(-2.25, -18) * mm});
            skLineSegment(sketch, "E101.MirrorCS", {"start": v(-2.25, -18) * mm, "end": v(-2.25, -15) * mm});
            skLineSegment(sketch, "E102.MirrorCS", {"start": v(-3.75, -15) * mm, "end": v(-2.25, -15) * mm});
            skLineSegment(sketch, "E103.MirrorCS", {"start": v(-4.25, -23) * mm, "end": v(-4.25, -18) * mm});
            skLineSegment(sketch, "E104.MirrorCS", {"start": v(-4.25, -18) * mm, "end": v(-3.75, -18) * mm});
            skLineSegment(sketch, "E105.MirrorCS", {"start": v(-3.75, -17) * mm, "end": v(-3.75, -15) * mm});
            skSolve(sketch);
        }
        {
            var Q0;
            Q0=makeQuery(id+"F2.imprint","IMPRINT",FACE,{"disambiguationData":[TD([[makeQuery(id+"F2.imprint","IMPRINT",EDGE,{"derivedFrom":sQuery(id+"F2.wireOp",EDGE,"082e3635-987c-4050-8474-c287f25c8af8.MirrorCS")}),1.0]])]});
            var Q1;
            Q1=makeQuery(id+"F2.imprint","IMPRINT",FACE,{"disambiguationData":[TD([[makeQuery(id+"F2.imprint","IMPRINT",EDGE,{"derivedFrom":sQuery(id+"F2.wireOp",EDGE,"E84.bottom")}),1.0]])]});
            var Q2;
            Q2=makeQuery(id+"F2.imprint","IMPRINT",FACE,{"disambiguationData":[TD([[makeQuery(id+"F2.imprint","IMPRINT",EDGE,{"derivedFrom":sQuery(id+"F2.wireOp",EDGE,"E96.MirrorCS")}),1.0]])]});
            extrude(context, id + "F3", {"entities" : qUnion([Q0, Q1, Q2]), "operationType" : NewBodyOperationType.ADD, "depth" : 3.25 * mm});
        }
        {
            var Q0;
            Q0=makeQuery(id+"F3.opExtrude","CAP_FACE",FACE,{"disambiguationData":[OSD([sQuery(id+"F2.wireOp",EDGE,"E96.MirrorCS"),sQuery(id+"F2.wireOp",EDGE,"E97.MirrorCS"),sQuery(id+"F2.wireOp",EDGE,"E98.MirrorCS"),sQuery(id+"F2.wireOp",EDGE,"E99.MirrorCS"),sQuery(id+"F2.wireOp",EDGE,"E100.MirrorCS"),sQuery(id+"F2.wireOp",EDGE,"E101.MirrorCS"),sQuery(id+"F2.wireOp",EDGE,"E102.MirrorCS"),sQuery(id+"F2.wireOp",EDGE,"E103.MirrorCS"),sQuery(id+"F2.wireOp",EDGE,"E104.MirrorCS"),sQuery(id+"F2.wireOp",EDGE,"E105.MirrorCS")])],"isStart":false});
            var sketch = newSketch(context, id + "F4", { "sketchPlane" : qUnion([Q0])});
            skLineSegment(sketch, "E106", {"start": v(2.75, -17) * mm, "end": v(-2.75, -17) * mm, "construction": true});
            skPoint(sketch, "E107", {"position": v(0, -17) * mm});
            skLineSegment(sketch, "E108", {"start": v(0, -17) * mm, "end": v(0, -22.48) * mm, "construction": true});
            skLineSegment(sketch, "E109.MirrorCS", {"start": v(-2.75, -23) * mm, "end": v(-2.75, -17) * mm});
            skLineSegment(sketch, "E110.MirrorCS", {"start": v(-5.75, -17) * mm, "end": v(-2.75, -17) * mm});
            skLineSegment(sketch, "E111.MirrorCS", {"start": v(-5.75, -23) * mm, "end": v(-5.75, -17) * mm});
            skLineSegment(sketch, "E112.MirrorCS", {"start": v(-5.75, -23) * mm, "end": v(-2.75, -23) * mm});
            skLineSegment(sketch, "E113.MirrorCS", {"start": v(2.75, -23) * mm, "end": v(2.75, -17) * mm});
            skLineSegment(sketch, "E114.MirrorCS", {"start": v(5.75, -23) * mm, "end": v(2.75, -23) * mm});
            skLineSegment(sketch, "E115.MirrorCS", {"start": v(5.75, -23) * mm, "end": v(5.75, -17) * mm});
            skLineSegment(sketch, "E116.MirrorCS", {"start": v(5.75, -17) * mm, "end": v(2.75, -17) * mm});
            skSolve(sketch);
        }
        {
            var Q0;
            Q0=makeQuery(id+"F4.imprint","IMPRINT",FACE,{"disambiguationData":[TD([[makeQuery(id+"F4.imprint","IMPRINT",EDGE,{"derivedFrom":sQuery(id+"F4.wireOp",EDGE,"E111.MirrorCS")}),-1.0]])]});
            var Q1;
            {var subQ1=sQuery(id+"F4.wireOp",EDGE,"ee415b56-a3a5-43e7-b2b9-08c54a094791.MirrorCS");Q1=makeQuery(id+"F4.imprint","IMPRINT",FACE,{"disambiguationData":[TD([[makeQuery(id+"F4.imprint","IMPRINT",EDGE,{"derivedFrom":subQ1}),-1.0]])]});}
            var Q2;
            Q2=makeQuery(id+"F4.imprint","IMPRINT",FACE,{"disambiguationData":[TD([[makeQuery(id+"F4.imprint","IMPRINT",EDGE,{"derivedFrom":sQuery(id+"F4.wireOp",EDGE,"4d7947e5-259c-42fd-9370-be67d3335575.bottom")}),1.0]])]});
            var Q3;
            {var subQ5=makeQuery(id+"F3.opExtrude","CAP_EDGE",EDGE,{"disambiguationData":[OSD([sQuery(id+"F2.wireOp",EDGE,"E103.MirrorCS")])],"isStart":false});Q3=makeQuery(id+"F4.imprint","IMPRINT",FACE,{"disambiguationData":[TD([[makeQuery(id+"F4.imprint","IMPRINT",EDGE,{"derivedFrom":subQ5}),-1.0]])]});}
            var Q4;
            Q4=makeQuery(id+"F4.imprint","IMPRINT",FACE,{"disambiguationData":[TD([[makeQuery(id+"F4.imprint","IMPRINT",EDGE,{"derivedFrom":sQuery(id+"F4.wireOp",EDGE,"E113.MirrorCS")}),-1.0]])]});
            extrude(context, id + "F5", {"entities" : qUnion([Q0, Q1, Q2, Q3, Q4]), "operationType" : NewBodyOperationType.ADD, "depth" : 2 * mm});
        }
        {
            var Q0;
            Q0=makeQuery(id+"F1.opExtrude","CAP_FACE",FACE,{"disambiguationData":[OSD([sQuery(id+"F0.wireOp",EDGE,"E0.filletArc"),sQuery(id+"F0.wireOp",EDGE,"E1.filletArc"),sQuery(id+"F0.wireOp",EDGE,"E2.filletArc"),sQuery(id+"F0.wireOp",EDGE,"E3.filletArc"),sQuery(id+"F0.wireOp",EDGE,"E4"),sQuery(id+"F0.wireOp",EDGE,"E5.MirrorC"),sQuery(id+"F0.wireOp",EDGE,"E6.MirrorC"),sQuery(id+"F0.wireOp",EDGE,"E7.MirrorC"),sQuery(id+"F0.wireOp",EDGE,"E8"),sQuery(id+"F0.wireOp",EDGE,"E9"),sQuery(id+"F0.wireOp",EDGE,"E10"),sQuery(id+"F0.wireOp",EDGE,"E11"),sQuery(id+"F0.wireOp",EDGE,"E12"),sQuery(id+"F0.wireOp",EDGE,"E13"),sQuery(id+"F0.wireOp",EDGE,"E14"),sQuery(id+"F0.wireOp",EDGE,"E15"),sQuery(id+"F0.wireOp",EDGE,"E16"),sQuery(id+"F0.wireOp",EDGE,"E17"),sQuery(id+"F0.wireOp",EDGE,"E18"),sQuery(id+"F0.wireOp",EDGE,"E19"),sQuery(id+"F0.wireOp",EDGE,"E20"),sQuery(id+"F0.wireOp",EDGE,"E21"),sQuery(id+"F0.wireOp",EDGE,"E22"),sQuery(id+"F0.wireOp",EDGE,"E23"),sQuery(id+"F0.wireOp",EDGE,"E24"),sQuery(id+"F0.wireOp",EDGE,"E25"),sQuery(id+"F0.wireOp",EDGE,"E26"),sQuery(id+"F0.wireOp",EDGE,"E27"),sQuery(id+"F0.wireOp",EDGE,"E32.5"),sQuery(id+"F0.wireOp",EDGE,"E32.12"),sQuery(id+"F0.wireOp",EDGE,"E32.13"),sQuery(id+"F0.wireOp",EDGE,"E32.19"),sQuery(id+"F0.wireOp",EDGE,"E33"),sQuery(id+"F0.wireOp",EDGE,"E34"),sQuery(id+"F0.wireOp",EDGE,"E35"),sQuery(id+"F0.wireOp",EDGE,"E36"),sQuery(id+"F0.wireOp",EDGE,"E37"),sQuery(id+"F0.wireOp",EDGE,"E38"),sQuery(id+"F0.wireOp",EDGE,"E39"),sQuery(id+"F0.wireOp",EDGE,"E40"),sQuery(id+"F0.wireOp",EDGE,"E41"),sQuery(id+"F0.wireOp",EDGE,"E42"),sQuery(id+"F0.wireOp",EDGE,"E43.0"),sQuery(id+"F0.wireOp",EDGE,"E43.1"),sQuery(id+"F0.wireOp",EDGE,"E44.0.1.0"),sQuery(id+"F0.wireOp",EDGE,"E44.0.1.1"),sQuery(id+"F0.wireOp",EDGE,"E44.0.1.2"),sQuery(id+"F0.wireOp",EDGE,"E44.0.1.3"),sQuery(id+"F0.wireOp",EDGE,"E44.0.2.0"),sQuery(id+"F0.wireOp",EDGE,"E44.0.2.1"),sQuery(id+"F0.wireOp",EDGE,"E44.0.2.2"),sQuery(id+"F0.wireOp",EDGE,"E44.0.2.3"),sQuery(id+"F0.wireOp",EDGE,"E44.0.3.2"),sQuery(id+"F0.wireOp",EDGE,"E44.0.3.3"),sQuery(id+"F0.wireOp",EDGE,"E45.0.1.0"),sQuery(id+"F0.wireOp",EDGE,"E45.0.1.1"),sQuery(id+"F0.wireOp",EDGE,"E45.0.1.2"),sQuery(id+"F0.wireOp",EDGE,"E45.0.1.3"),sQuery(id+"F0.wireOp",EDGE,"E49.trimOffspring"),sQuery(id+"F0.wireOp",EDGE,"E50.trimOffspring"),sQuery(id+"F0.wireOp",EDGE,"E54.left"),sQuery(id+"F0.wireOp",EDGE,"E54.right"),sQuery(id+"F0.wireOp",EDGE,"xoITrzZp-boxu-zUea-Kb7O-LUEDmCAUrp8Y"),sQuery(id+"F0.wireOp",EDGE,"arG5BOlZ-v33J-HKLe-jAwC-aBxCeF4Obx18")])],"isStart":true});
            var Q1;
            Q1=makeQuery(id+"F1.opExtrude","CAP_FACE",FACE,{"disambiguationData":[OSD([sQuery(id+"F0.wireOp",EDGE,"E0.filletArc"),sQuery(id+"F0.wireOp",EDGE,"E1.filletArc"),sQuery(id+"F0.wireOp",EDGE,"E2.filletArc"),sQuery(id+"F0.wireOp",EDGE,"E3.filletArc"),sQuery(id+"F0.wireOp",EDGE,"E4"),sQuery(id+"F0.wireOp",EDGE,"E5.MirrorC"),sQuery(id+"F0.wireOp",EDGE,"E6.MirrorC"),sQuery(id+"F0.wireOp",EDGE,"E7.MirrorC"),sQuery(id+"F0.wireOp",EDGE,"E8"),sQuery(id+"F0.wireOp",EDGE,"E9"),sQuery(id+"F0.wireOp",EDGE,"E10"),sQuery(id+"F0.wireOp",EDGE,"E11"),sQuery(id+"F0.wireOp",EDGE,"E12"),sQuery(id+"F0.wireOp",EDGE,"E13"),sQuery(id+"F0.wireOp",EDGE,"E14"),sQuery(id+"F0.wireOp",EDGE,"E15"),sQuery(id+"F0.wireOp",EDGE,"E16"),sQuery(id+"F0.wireOp",EDGE,"E17"),sQuery(id+"F0.wireOp",EDGE,"E18"),sQuery(id+"F0.wireOp",EDGE,"E19"),sQuery(id+"F0.wireOp",EDGE,"E20"),sQuery(id+"F0.wireOp",EDGE,"E21"),sQuery(id+"F0.wireOp",EDGE,"E22"),sQuery(id+"F0.wireOp",EDGE,"E23"),sQuery(id+"F0.wireOp",EDGE,"E24"),sQuery(id+"F0.wireOp",EDGE,"E25"),sQuery(id+"F0.wireOp",EDGE,"E26"),sQuery(id+"F0.wireOp",EDGE,"E27"),sQuery(id+"F0.wireOp",EDGE,"E32.5"),sQuery(id+"F0.wireOp",EDGE,"E32.12"),sQuery(id+"F0.wireOp",EDGE,"E32.13"),sQuery(id+"F0.wireOp",EDGE,"E32.19"),sQuery(id+"F0.wireOp",EDGE,"E33"),sQuery(id+"F0.wireOp",EDGE,"E34"),sQuery(id+"F0.wireOp",EDGE,"E35"),sQuery(id+"F0.wireOp",EDGE,"E36"),sQuery(id+"F0.wireOp",EDGE,"E37"),sQuery(id+"F0.wireOp",EDGE,"E38"),sQuery(id+"F0.wireOp",EDGE,"E39"),sQuery(id+"F0.wireOp",EDGE,"E40"),sQuery(id+"F0.wireOp",EDGE,"E41"),sQuery(id+"F0.wireOp",EDGE,"E42"),sQuery(id+"F0.wireOp",EDGE,"E43.0"),sQuery(id+"F0.wireOp",EDGE,"E43.1"),sQuery(id+"F0.wireOp",EDGE,"E44.0.1.0"),sQuery(id+"F0.wireOp",EDGE,"E44.0.1.1"),sQuery(id+"F0.wireOp",EDGE,"E44.0.1.2"),sQuery(id+"F0.wireOp",EDGE,"E44.0.1.3"),sQuery(id+"F0.wireOp",EDGE,"E44.0.2.0"),sQuery(id+"F0.wireOp",EDGE,"E44.0.2.1"),sQuery(id+"F0.wireOp",EDGE,"E44.0.2.2"),sQuery(id+"F0.wireOp",EDGE,"E44.0.2.3"),sQuery(id+"F0.wireOp",EDGE,"E44.0.3.2"),sQuery(id+"F0.wireOp",EDGE,"E44.0.3.3"),sQuery(id+"F0.wireOp",EDGE,"E45.0.1.0"),sQuery(id+"F0.wireOp",EDGE,"E45.0.1.1"),sQuery(id+"F0.wireOp",EDGE,"E45.0.1.2"),sQuery(id+"F0.wireOp",EDGE,"E45.0.1.3"),sQuery(id+"F0.wireOp",EDGE,"E49.trimOffspring"),sQuery(id+"F0.wireOp",EDGE,"E50.trimOffspring"),sQuery(id+"F0.wireOp",EDGE,"E54.left"),sQuery(id+"F0.wireOp",EDGE,"E54.right"),sQuery(id+"F0.wireOp",EDGE,"E62"),sQuery(id+"F0.wireOp",EDGE,"E63.MirrorCS")])],"isStart":false});
            var Q2;
            Q2=makeQuery(id+"F5.opExtrude","CAP_FACE",FACE,{"disambiguationData":[OSD([sQuery(id+"F2.wireOp",EDGE,"E100.MirrorCS"),sQuery(id+"F2.wireOp",EDGE,"E103.MirrorCS"),sQuery(id+"F2.wireOp",EDGE,"E104.MirrorCS"),sQuery(id+"F4.wireOp",EDGE,"E109.MirrorCS"),sQuery(id+"F4.wireOp",EDGE,"E110.MirrorCS"),sQuery(id+"F4.wireOp",EDGE,"E111.MirrorCS"),sQuery(id+"F4.wireOp",EDGE,"E112.MirrorCS")])],"isStart":false});
            var Q3;
            Q3=makeQuery(id+"F5.opExtrude","CAP_FACE",FACE,{"disambiguationData":[OSD([sQuery(id+"F4.wireOp",EDGE,"E113.MirrorCS"),sQuery(id+"F4.wireOp",EDGE,"E114.MirrorCS"),sQuery(id+"F4.wireOp",EDGE,"E115.MirrorCS"),sQuery(id+"F4.wireOp",EDGE,"E116.MirrorCS")])],"isStart":false});
            var Q4;
            Q4=makeQuery(id+"F5.boolean.opBoolean","MERGE",FACE,{"derivedFrom":[makeQuery(id+"F3.opExtrude","SWEPT_FACE",FACE,{"disambiguationData":[OSD([sQuery(id+"F2.wireOp",EDGE,"E98.MirrorCS"),sQuery(id+"F2.wireOp",EDGE,"E99.MirrorCS")])]}),makeQuery(id+"F5.opExtrude","SWEPT_FACE",FACE,{"disambiguationData":[OSD([sQuery(id+"F4.wireOp",EDGE,"E110.MirrorCS")])]})]});
            var Q5;
            Q5=makeQuery(id+"F5.boolean.opBoolean","MERGE",FACE,{"derivedFrom":[makeQuery(id+"F3.opExtrude","SWEPT_FACE",FACE,{"disambiguationData":[OSD([sQuery(id+"F2.wireOp",EDGE,"E84.right"),sQuery(id+"F2.wireOp",EDGE,"E85.right")])]}),makeQuery(id+"F5.opExtrude","SWEPT_FACE",FACE,{"disambiguationData":[OSD([sQuery(id+"F4.wireOp",EDGE,"E116.MirrorCS")])]})]});
            var Q6;
            Q6=makeQuery(id+"F3.opExtrude","SWEPT_FACE",FACE,{"disambiguationData":[OSD([sQuery(id+"F2.wireOp",EDGE,"E86.right")])]});
            var Q7;
            Q7=makeQuery(id+"F3.opExtrude","SWEPT_FACE",FACE,{"disambiguationData":[OSD([sQuery(id+"F2.wireOp",EDGE,"E102.MirrorCS")])]});
            var Q8;
            Q8=makeQuery(id+"F5.boolean.opBoolean","MERGE",FACE,{"derivedFrom":[makeQuery(id+"F3.opExtrude","SWEPT_FACE",FACE,{"disambiguationData":[OSD([sQuery(id+"F2.wireOp",EDGE,"E96.MirrorCS")])]}),makeQuery(id+"F5.opExtrude","SWEPT_FACE",FACE,{"disambiguationData":[OSD([sQuery(id+"F4.wireOp",EDGE,"E112.MirrorCS")])]})]});
            var Q9;
            Q9=makeQuery(id+"F5.boolean.opBoolean","MERGE",FACE,{"derivedFrom":[makeQuery(id+"F3.opExtrude","SWEPT_FACE",FACE,{"disambiguationData":[OSD([sQuery(id+"F2.wireOp",EDGE,"E84.left")])]}),makeQuery(id+"F5.opExtrude","SWEPT_FACE",FACE,{"disambiguationData":[OSD([sQuery(id+"F4.wireOp",EDGE,"E114.MirrorCS")])]})]});
            fillet(context, id + "F6", {"entities" : qUnion([Q0, Q1, Q2, Q3, Q4, Q5, Q6, Q7, Q8, Q9]), "radius" : .5 * mm, "tangentPropagation" : true, "allowEdgeOverflow" : false});
        }
        {
            var Q0;
            {var subQ0=sQuery(id+"F0.wireOp",EDGE,"E9");Q0=makeQuery(id+"F0.imprint","IMPRINT",FACE,{"disambiguationData":[TD([[makeQuery(id+"F0.imprint","IMPRINT",EDGE,{"derivedFrom":subQ0}),-1.0]])]});}
            var Q1;
            Q1=makeQuery(id+"F0.imprint","IMPRINT",FACE,{"disambiguationData":[TD([[makeQuery(id+"F0.imprint","IMPRINT",EDGE,{"derivedFrom":sQuery(id+"F0.wireOp",EDGE,"E11")}),-1.0]])]});
            var Q2;
            {var subQ0=sQuery(id+"F0.wireOp",EDGE,"E16");Q2=makeQuery(id+"F0.imprint","IMPRINT",FACE,{"disambiguationData":[TD([[makeQuery(id+"F0.imprint","IMPRINT",EDGE,{"derivedFrom":subQ0}),-1.0]])]});}
            var Q3;
            {var subQ0=sQuery(id+"F0.wireOp",EDGE,"E13");Q3=makeQuery(id+"F0.imprint","IMPRINT",FACE,{"disambiguationData":[TD([[makeQuery(id+"F0.imprint","IMPRINT",EDGE,{"derivedFrom":subQ0}),1.0]])]});}
            extrude(context, id + "F7", {"entities" : qUnion([Q0, Q1, Q2, Q3]), "operationType" : NewBodyOperationType.ADD, "depth" : 4 * mm});
        }
    });
